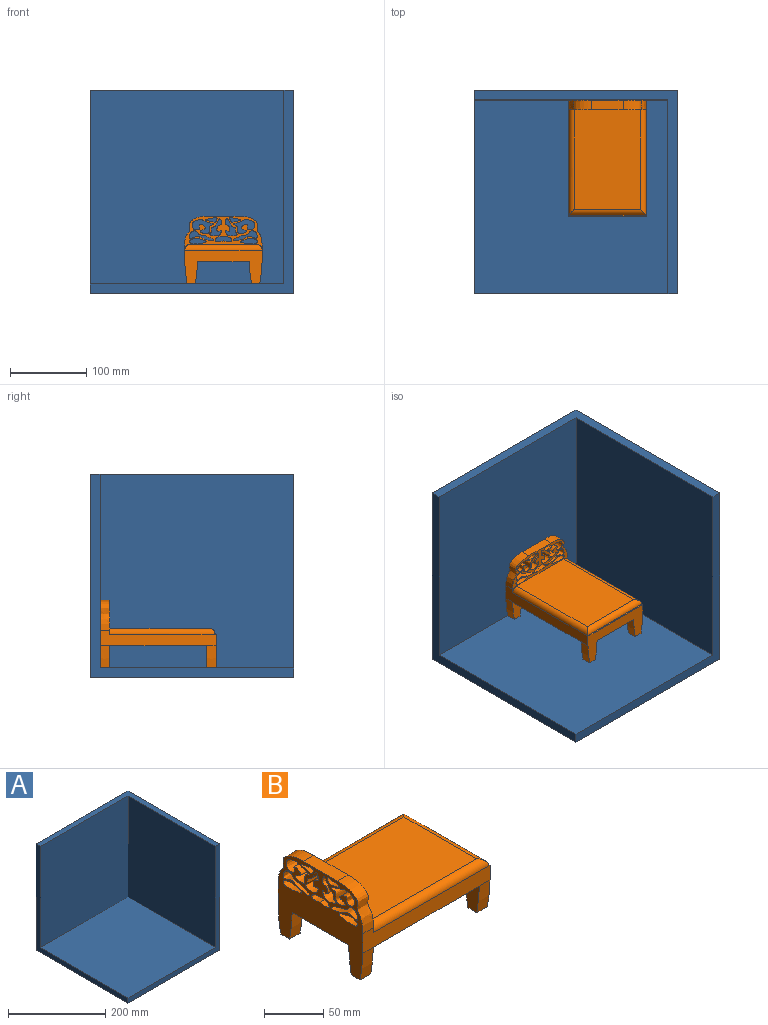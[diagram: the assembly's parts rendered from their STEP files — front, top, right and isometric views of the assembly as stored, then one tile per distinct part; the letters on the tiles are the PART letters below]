
ASSEMBLY  parts=2 mates=2
PART A: 9 faces, bbox 266.7x266.7x266.7 mm
  f0: plane 266.7x266.7mm, normal (0,-1,0), area 6612.9mm2, adj f1,f3,f4,f5,f7,f8
  f1: plane 266.7x266.7mm, normal (0,0,1), area 6612.9mm2, adj f0,f2,f3,f4,f6,f7
  f2: plane 266.7x266.7mm, normal (0,1,0), area 71128.9mm2, adj f1,f3,f4,f5
  f3: plane 266.7x266.7mm, normal (-1,0,0), area 6612.9mm2, adj f0,f1,f2,f5,f6,f8
  f4: plane 266.7x266.7mm, normal (1,0,0), area 71128.9mm2, adj f0,f1,f2,f5
  f5: plane 266.7x266.7mm, normal (0,0,-1), area 71128.9mm2, adj f0,f2,f3,f4
  f6: plane 254x254mm, normal (0,-1,0), area 64516mm2, adj f1,f3,f7,f8
  f7: plane 254x254mm, normal (-1,0,0), area 64516mm2, adj f0,f1,f6,f8
  f8: plane 254x254mm, normal (0,0,1), area 64516mm2, adj f0,f3,f6,f7
PART B: 44 faces, bbox 152.4x101.8x88.9 mm
  f0: plane 101.82x44.42mm, normal (1,0,0), area 1719mm2, adj f2,f12,f13,f24,f26,f28,f29,f30
  f1: plane 101.82x88.9mm, normal (-1,0,0), area 4845.9mm2, adj f2,f10,f11,f12,f13,f14,f16,f17
  f2: plane 41.01x12.7mm, normal (0,0,1), area 520.9mm2, adj f0,f1,f29,f32
  f3: plane 29.21x17mm, normal (1,0,0), area 425.6mm2, adj f10,f14,f18,f19
  f4: plane 29.21x17mm, normal (1,0,0), area 425.6mm2, adj f11,f14,f16,f17
  f5: plane 29.21x17mm, normal (-1,0,0), area 425.6mm2, adj f7,f14,f20,f23
  f6: plane 29.21x17mm, normal (-1,0,0), area 425.6mm2, adj f8,f14,f21,f22
  f7: plane 12.7x10.75mm, normal (0,0,-1), area 136.5mm2, adj f5,f9,f20,f23
  f8: plane 12.7x10.75mm, normal (0,0,-1), area 136.5mm2, adj f6,f9,f21,f22
  f9: plane 101.6x44.45mm, normal (1,0,0), area 2399.5mm2, adj f7,f8,f12,f13,f14,f15,f20,f21
  f10: plane 12.7x10.75mm, normal (0,0,-1), area 136.5mm2, adj f1,f3,f18,f19
  f11: plane 12.7x10.75mm, normal (0,0,-1), area 136.5mm2, adj f1,f4,f16,f17
  f12: plane 152.4x20.36mm, normal (0,-1,0), area 2391.7mm2, adj f0,f1,f9,f14,f15,f19,f23,f25
  f13: plane 152.4x20.36mm, normal (0,1,0), area 2391.7mm2, adj f0,f1,f9,f14,f15,f16,f22,f25
  f14: plane 152.4x101.6mm, normal (0,0,-1), area 14620.4mm2, adj f1,f3,f4,f5,f6,f9,f12,f13
  f15: plane 101.6x1.52mm, normal (0,0,1), area 154.8mm2, adj f9,f12,f13,f25
  f16: extruded ~29.21x12.7mm, area 373.4mm2, adj f1,f4,f11,f13
  f17: extruded ~29.21x12.7mm, area 373.4mm2, adj f1,f4,f11,f14
  f18: extruded ~29.21x12.7mm, area 373.4mm2, adj f1,f3,f10,f14
  f19: extruded ~29.21x12.7mm, area 373.4mm2, adj f1,f3,f10,f12
  f20: extruded ~29.21x12.7mm, area 373.4mm2, adj f5,f7,f9,f14
  f21: extruded ~29.21x12.7mm, area 373.4mm2, adj f6,f8,f9,f14
  f22: extruded ~29.21x12.7mm, area 373.4mm2, adj f6,f8,f9,f13
  f23: extruded ~29.21x12.7mm, area 373.4mm2, adj f5,f7,f9,f12
  f24: plane 130.82x86.88mm, normal (0,0,1), area 11365.8mm2, adj f0,f26,f27,f28
  f25: plane 101.6x0.03mm, normal (1,0,0), area 3mm2, adj f12,f13,f15,f27
  f26: cylinder r=7.36mm len=138.18mm, axis (1,0,0), area 1566.2mm2, adj f0,f13,f24,f27
  f27: cylinder r=7.36mm len=101.6mm, axis (0,1,0), area 1112.6mm2, adj f24,f25,f26,f28
  f28: cylinder r=7.36mm len=138.18mm, axis (-1,0,0), area 1566.2mm2, adj f0,f12,f24,f27
  f29: extruded ~39.33x30.29mm, area 743.7mm2, adj f0,f1,f2,f12
  f30: extruded ~31.64x13.04mm, area 933.6mm2, adj f0,f1
  f31: extruded ~27.36x18.24mm, area 1201mm2, adj f0,f1
  f32: extruded ~39.33x30.29mm, area 743.7mm2, adj f0,f1,f2,f13
  f33: extruded ~22.02x12.7mm, area 614.7mm2, adj f0,f1
  f34: extruded ~22.21x15.43mm, area 912.4mm2, adj f0,f1
  f35: extruded ~22.02x12.7mm, area 614.7mm2, adj f0,f1
  f36: extruded ~27.36x18.24mm, area 1201mm2, adj f0,f1
  f37: extruded ~31.64x13.04mm, area 933.6mm2, adj f0,f1
  f38: extruded ~22.21x15.43mm, area 912.4mm2, adj f0,f1
  f39: extruded ~14.46x12.7mm, area 428.6mm2, adj f0,f1
  f40: extruded ~12.7x10.43mm, area 272.5mm2, adj f0,f1,f41,f42
  f41: extruded ~12.7x10.43mm, area 272.5mm2, adj f0,f1,f40,f42
  f42: plane 12.7x6mm, normal (0,0,-1), area 76.1mm2, adj f0,f1,f40,f41
  f43: extruded ~14.46x12.7mm, area 428.6mm2, adj f0,f1
PLACE A t=(-154.45,-25.72,32.49)mm fixed
PLACE B rot(axis=(0,0,-1),90deg) t=(-56.61,40.03,99.46)mm
MATE planar A.f6 <-> B.f1  axis (0,-1,0) through (-154.96,121.43,172.19)mm
MATE planar A.f8 <-> B.f10  axis (0,0,1) through (-154.96,-5.57,45.19)mm
